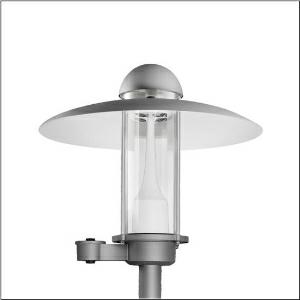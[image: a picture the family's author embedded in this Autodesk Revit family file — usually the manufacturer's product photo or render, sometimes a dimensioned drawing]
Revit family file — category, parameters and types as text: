
# Revit family: city-light_elegance_iq___st1_2a_5xa5265ev14h000022_6cf2
name_source: partatom
category: Lighting Fixtures
units: mm (PartAtom-declared; Revit-internal decimal feet)

## family parameters
Cut with Voids When Loaded = No
Host = Face
Light Source = No
Part Type = Normal
Room Calculation Point = No
Round Connector Dimension = Use Diameter
Shared = No

## types (1)
- --- (1 x LED, 1460 lm, 10.7 W, 3000K)
    Apparent Load = 11 VA
    CIE Flux Codes = 22 62 94 98 100
    Color Rendering = 70
    Color Temperature = 3000K
    Default Elevation = 1800 mm
    Description = City-Light Elegance iQ, mast luminaire, Module 540 iQ-SR, primary light control with 3 zone facetted reflector, of plastic, silver coated, highly specular, structured, primary optical cover: cover, of PMMA, transparent, light distribution: ST1.2a, light emission: direct distribution, primary light characteristic: asymmetric, installation type: post-top, LED, High Power LED, rated luminous flux: 1.460lm, luminous efficacy: 136lm/W, light colour: 730, colour temperature: 3000K, control gear: iQ-Street Remote, D4i with power reduction, control: optimised constant luminous flux control (CLO 2.0), Desk-Remote (wireless, voltage-free reading and setting of iQ features in the workshop via application-optimized NFC function/RFID function), Light-Fading, Smart-Wire, Night-Set, Lumen-Switch, Temp-Guard, Auto-Match, Street-Remote, pre-setting: logarithmic dimming characteristic, with terminal, 6-pole, max. 2.5mm², mains connection: 230..240V, AC, 50/60Hz, connection cable pre-assembled, cable length: 5,5m, wiring characteristics: H07RN-F, start of lifetime: 11W, end of service life: 11W, reduction: 6W, luminaire housing, upper part, of aluminium, coated, Siteco® metallic grey (DB 702S), diameter: 750mm, height: 675mm, spigot size: d x l = 76 x 70mm (post-top) | with reducer (optional accessory) 60 x 70mm, mounting height: 3..5m, post-top mast mounting element, of diecast aluminium, coated, Siteco® metallic grey (DB 702S), Module 540 iQ-SR, traffic white (RAL 9016), equipment: standard, Smart Interface above, protection rating (complete): IP65, insulation class (complete): insulation class II (safety insulation), certification: CE, ENEC, VDE, packaging unit: 1 piece

Light Distribution: ST1.2a
    Height = 675 mm
    Lamp = 1 x LED
    Lamp Light Flux = 1460 lm
    Lamp Power = 10.7 W
    Lamp count = 1
    Length = 750 mm
    Luminous efficacy = 136 lm/W
    Manufacturer = Siteco
    ModVariant = No
    Model = 5XA5265EV14H000022
    Number of Poles = 1
    OnlyDefault = Yes
    Power Factor = 1
    Product Name = City-Light Elegance iQ | ST1.2a
    Product group = mast luminaire | pylon top
    ProductGroupID = 6100
    Protection Class = Protection class II
    Protection Degree = IP 65
    RLX_Detail_Level = 1
    RLX_Emergency_Light_Flux = 0 lm
    RLX_Emergency_Type = 0
    RLX_Emergency_Type_DB = No
    RlxData = <blob elided: 72957 chars, md5=cd7fe5ae>
    Socket = socket
    Standby Power = 0 W
    System Light Flux = 1460 lm
    System Power = 11 W
    Type Comments = factory setting: luminous flux: 100 % | dim-lin: 254 | 419 mA
    Type Image = l_1005991.jpg
    URL = http://relux.com
    VarID = @adj_086388
    Voltage = 0 V
    Weight = 0.00 kg
    Width = 0 mm  [stored 0 ft]

note: [stored X ft] marks values corroborated as IEEE doubles in the binary element streams (Revit-internal decimal feet)

## geometry (parser evidence)
native form markers: Blend x4, Sweep x9
no freeform markers — native parametric forms only
